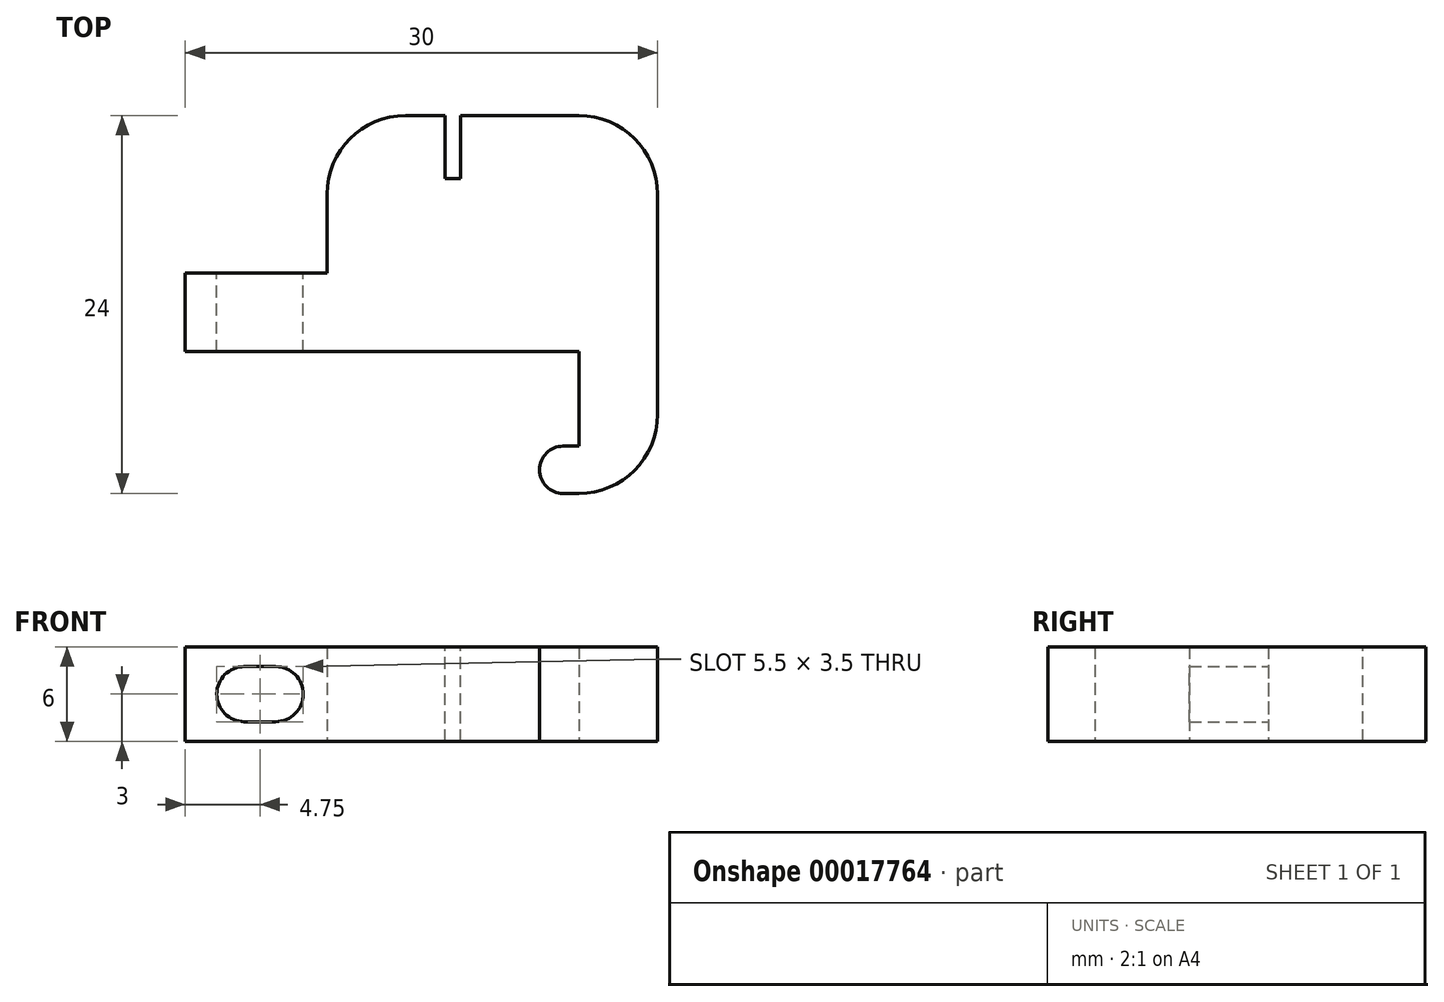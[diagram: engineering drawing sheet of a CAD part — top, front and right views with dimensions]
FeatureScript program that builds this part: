
annotation { "Feature Type Name" : "Feature", "Feature Type Description" : "" }
export const myFeature = defineFeature(function(context is Context, id is Id, definition is map)
    precondition{}
    {
        {
            var Q0;
            Q0=qCreatedBy(makeId("Top.planeOp"),FACE);
            var sketch = newSketch(context, id + "F0", { "sketchPlane" : qUnion([Q0])});
            skLineSegment(sketch, "E0", {"start": v(0, 0) * mm, "end": v(5, 0) * mm});
            skLineSegment(sketch, "E1", {"start": v(5, 0) * mm, "end": v(5, 14) * mm});
            skLineSegment(sketch, "E2", {"start": v(5, 14) * mm, "end": v(-25, 14) * mm});
            skLineSegment(sketch, "E3", {"start": v(-25, 14) * mm, "end": v(-25, 9) * mm});
            skLineSegment(sketch, "E4", {"start": v(-25, 9) * mm, "end": v(0, 9) * mm});
            skLineSegment(sketch, "E5", {"start": v(0, 9) * mm, "end": v(0, 3) * mm});
            skLineSegment(sketch, "E6", {"start": v(0, 3) * mm, "end": v(-1, 3) * mm});
            skLineSegment(sketch, "E7", {"start": v(0, 0) * mm, "end": v(-1, 0) * mm});
            skArc(sketch, "E8", {"start": v(-1, 3) * mm, "mid": v(-2.5, 1.5) * mm, "end": v(-1, 0) * mm});
            skSolve(sketch);
        }
        {
            var Q0;
            Q0=qSketchRegion(id+"F0",true);
            extrude(context, id + "F1", {"entities" : qUnion([Q0]), "depth" : 6 * mm});
        }
        {
            var Q0;
            Q0=makeQuery(id+"F1.opExtrude","SWEPT_FACE",FACE,{"disambiguationData":[OSD([sQuery(id+"F0.wireOp",EDGE,"E2")])]});
            var sketch = newSketch(context, id + "F2", { "sketchPlane" : qUnion([Q0])});
            skCircle(sketch, "E9", {"center": v(21.25, 3) * mm, "radius": 1.75 * mm});
            skLineSegment(sketch, "E10", {"start": v(21.25, 6) * mm, "end": v(21.25, 0) * mm});
            skCircle(sketch, "E11", {"center": v(19.25, 3) * mm, "radius": 1.75 * mm});
            skLineSegment(sketch, "E12", {"start": v(19.25, 4.75) * mm, "end": v(21.25, 4.75) * mm});
            skLineSegment(sketch, "E13", {"start": v(19.25, 1.25) * mm, "end": v(21.25, 1.25) * mm});
            skSolve(sketch);
        }
        {
            var Q0;
            Q0=qSketchRegion(id+"F2",true);
            var Q1;
            {var subQ0=sQuery(id+"F2.wireOp",EDGE,"E11");var subQ1=sQuery(id+"F2.wireOp",EDGE,"E9");var subQ3=makeQuery(id+"F2.imprint","INTERSECT",VERTEX,{"disambiguationData":[OD(0.0)],"derivedFrom":[subQ1,subQ0]});Q1=makeQuery(id+"F2.imprint","IMPRINT",FACE,{"disambiguationData":[TD([[makeQuery(id+"F2.imprint","IMPRINT",EDGE,{"disambiguationData":[TD([[subQ3,-1.0]])],"derivedFrom":subQ1}),1.0]])]});}
            extrude(context, id + "F3", {"entities" : qUnion([Q0, Q1]), "operationType" : NewBodyOperationType.REMOVE, "oppositeDirection" : true, "depth" : 25 * mm, "hasSecondDirection" : true, "secondDirectionOppositeDirection" : false, "secondDirectionDepth" : 25 * mm});
        }
        {
            var Q0;
            Q0=makeQuery(id+"F1.opExtrude","SWEPT_FACE",FACE,{"disambiguationData":[OSD([sQuery(id+"F0.wireOp",EDGE,"E2")])]});
            var sketch = newSketch(context, id + "F4", { "sketchPlane" : qUnion([Q0])});
            skLineSegment(sketch, "E14.bottom", {"start": v(-5, 6) * mm, "end": v(16, 6) * mm});
            skLineSegment(sketch, "E14.top", {"start": v(-5, 0) * mm, "end": v(16, 0) * mm});
            skLineSegment(sketch, "E14.left", {"start": v(-5, 6) * mm, "end": v(-5, 0) * mm});
            skLineSegment(sketch, "E14.right", {"start": v(16, 6) * mm, "end": v(16, 0) * mm});
            skLineSegment(sketch, "E15", {"start": v(16, 6) * mm, "end": v(10.64, 6) * mm, "construction": true});
            skLineSegment(sketch, "E16.0", {"start": v(8, 17.37) * mm, "end": v(8, -11.33) * mm, "construction": true});
            skSolve(sketch);
        }
        {
            var Q0;
            Q0=qSketchRegion(id+"F4",true);
            extrude(context, id + "F5", {"entities" : qUnion([Q0]), "operationType" : NewBodyOperationType.ADD, "depth" : 10 * mm});
        }
        {
            var Q0;
            Q0=makeQuery(id+"F5.opExtrude","CAP_EDGE",EDGE,{"disambiguationData":[OSD([sQuery(id+"F4.wireOp",EDGE,"E14.left")])],"isStart":false});
            var Q1;
            Q1=makeQuery(id+"F5.opExtrude","CAP_EDGE",EDGE,{"disambiguationData":[OSD([sQuery(id+"F4.wireOp",EDGE,"E14.right")])],"isStart":false});
            fillet(context, id + "F6", {"entities" : qUnion([Q0, Q1]), "radius" : 5 * mm, "tangentPropagation" : true, "allowEdgeOverflow" : false});
        }
        {
            var Q0;
            Q0=makeQuery(id+"F1.opExtrude","SWEPT_EDGE",EDGE,{"disambiguationData":[OSD([sQuery(id+"F0.wireOp",EDGE,"E0"),sQuery(id+"F0.wireOp",EDGE,"E1")])]});
            fillet(context, id + "F7", {"entities" : qUnion([Q0]), "radius" : 5 * mm, "tangentPropagation" : true, "allowEdgeOverflow" : false});
        }
        {
            var Q0;
            Q0=makeQuery(id+"F5.boolean.opBoolean","MERGE",FACE,{"derivedFrom":[makeQuery(id+"F1.opExtrude","CAP_FACE",FACE,{"disambiguationData":[OSD([sQuery(id+"F0.wireOp",EDGE,"E0"),sQuery(id+"F0.wireOp",EDGE,"E1"),sQuery(id+"F0.wireOp",EDGE,"E2"),sQuery(id+"F0.wireOp",EDGE,"E3"),sQuery(id+"F0.wireOp",EDGE,"E4"),sQuery(id+"F0.wireOp",EDGE,"E5"),sQuery(id+"F0.wireOp",EDGE,"E6"),sQuery(id+"F0.wireOp",EDGE,"E7"),sQuery(id+"F0.wireOp",EDGE,"E8")])],"isStart":false}),makeQuery(id+"F5.opExtrude","SWEPT_FACE",FACE,{"disambiguationData":[OSD([sQuery(id+"F4.wireOp",EDGE,"E14.bottom")])]})]});
            var sketch = newSketch(context, id + "F8", { "sketchPlane" : qUnion([Q0])});
            skLineSegment(sketch, "E17.0", {"start": v(-8, 27.06) * mm, "end": v(-8, 14) * mm, "construction": true});
            skLineSegment(sketch, "E18.0", {"start": v(-8.5, 27.06) * mm, "end": v(-8.5, 14) * mm, "construction": true});
            skLineSegment(sketch, "E19.0", {"start": v(-7.5, 27.06) * mm, "end": v(-7.5, 14) * mm, "construction": true});
            skLineSegment(sketch, "E20.0", {"start": v(0, 20) * mm, "end": v(-11, 20) * mm, "construction": true});
            skLineSegment(sketch, "E21", {"start": v(-8.5, 24) * mm, "end": v(-8.5, 20) * mm});
            skLineSegment(sketch, "E22", {"start": v(-8.5, 20) * mm, "end": v(-7.5, 20) * mm});
            skLineSegment(sketch, "E23", {"start": v(-7.5, 20) * mm, "end": v(-7.5, 24) * mm});
            skLineSegment(sketch, "E24", {"start": v(-7.5, 24) * mm, "end": v(-7.5, 27.06) * mm});
            skLineSegment(sketch, "E25", {"start": v(-8.5, 24) * mm, "end": v(-8.5, 27.06) * mm});
            skLineSegment(sketch, "E26", {"start": v(-8.5, 27.06) * mm, "end": v(-7.5, 27.06) * mm});
            skSolve(sketch);
        }
        {
            var Q0;
            {var subQ2=sQuery(id+"F8.wireOp",EDGE,"E21");Q0=makeQuery(id+"F8.imprint","IMPRINT",FACE,{"disambiguationData":[TD([[makeQuery(id+"F8.imprint","IMPRINT",EDGE,{"derivedFrom":subQ2}),1.0]])]});}
            extrude(context, id + "F9", {"entities" : qUnion([Q0]), "operationType" : NewBodyOperationType.REMOVE, "oppositeDirection" : true, "depth" : 25 * mm});
        }
    });
